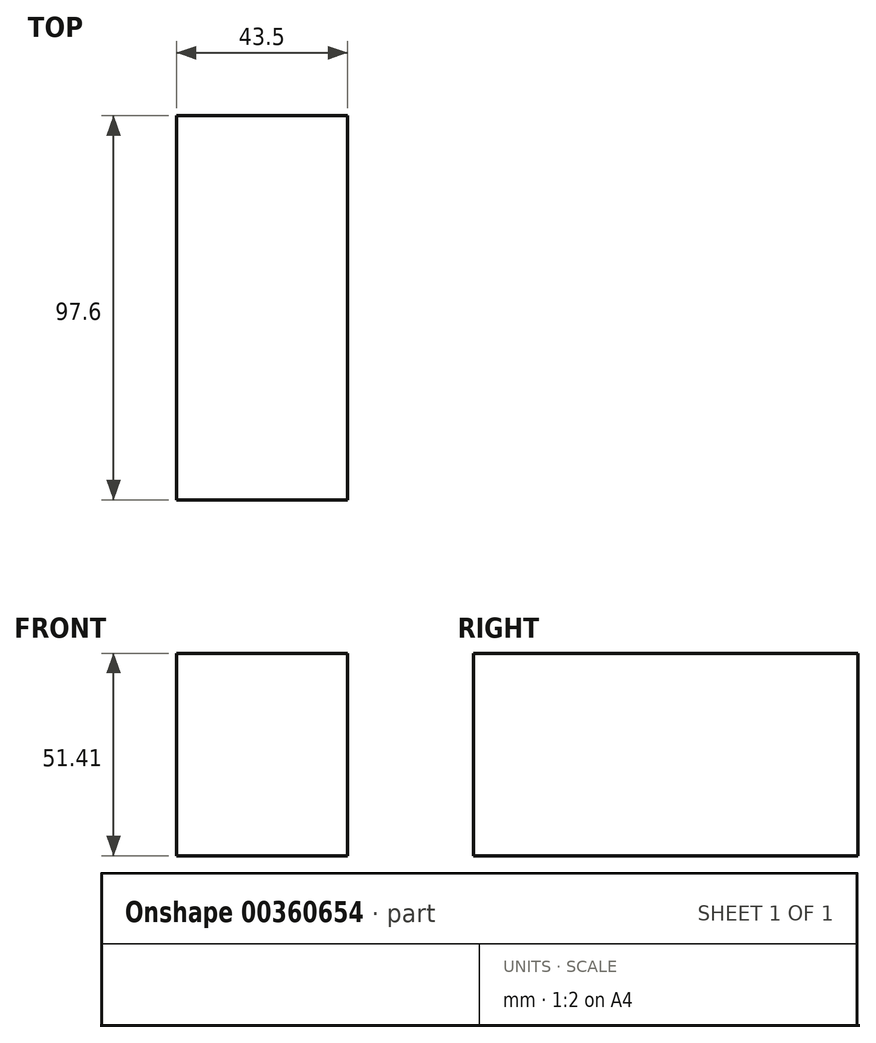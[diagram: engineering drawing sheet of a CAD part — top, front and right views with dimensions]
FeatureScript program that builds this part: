
annotation { "Feature Type Name" : "Feature", "Feature Type Description" : "" }
export const myFeature = defineFeature(function(context is Context, id is Id, definition is map)
    precondition{}
    {
        {
            var Q0;
            Q0=qCreatedBy(makeId("Front.planeOp"),FACE);
            var sketch = newSketch(context, id + "F0", { "sketchPlane" : qUnion([Q0])});
            skLineSegment(sketch, "E0.bottom", {"start": v(-18.1, 32.4) * mm, "end": v(25.4, 32.4) * mm});
            skLineSegment(sketch, "E0.top", {"start": v(-18.1, -19.02) * mm, "end": v(25.4, -19.02) * mm});
            skLineSegment(sketch, "E0.left", {"start": v(-18.1, 32.4) * mm, "end": v(-18.1, -19.02) * mm});
            skLineSegment(sketch, "E0.right", {"start": v(25.4, 32.4) * mm, "end": v(25.4, -19.02) * mm});
            skSolve(sketch);
        }
        {
            var Q0;
            Q0 = qSketchRegion(id + "F0", true);
            extrude(context, id + "F1", {"entities" : qUnion([Q0]), "depth" : 97.6 * mm});
        }
    });
